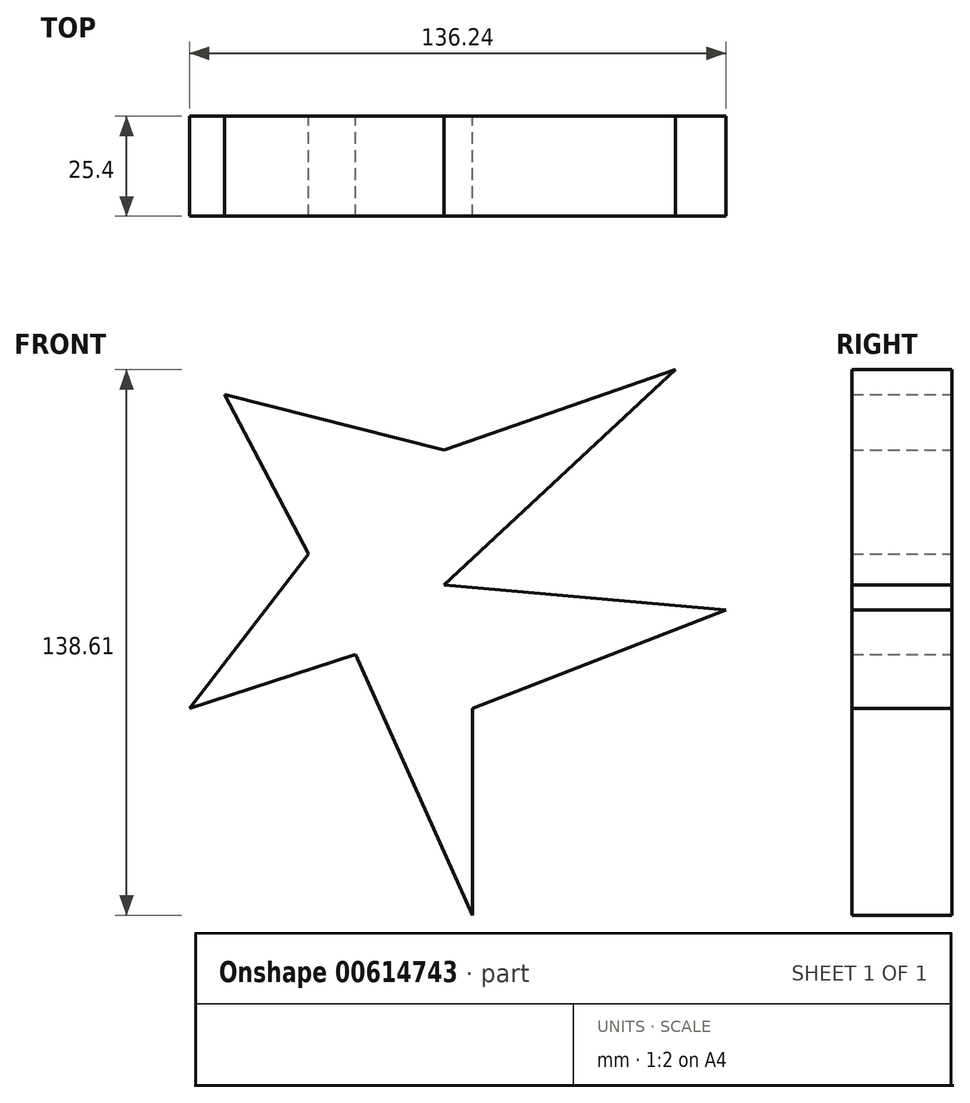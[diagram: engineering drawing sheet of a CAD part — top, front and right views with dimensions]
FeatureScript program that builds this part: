
annotation { "Feature Type Name" : "Feature", "Feature Type Description" : "" }
export const myFeature = defineFeature(function(context is Context, id is Id, definition is map)
    precondition{}
    {
        {
            var Q0;
            Q0=qCreatedBy(makeId("Front.planeOp"),FACE);
            var sketch = newSketch(context, id + "F0", { "sketchPlane" : qUnion([Q0])});
            skLineSegment(sketch, "E0", {"start": v(0, 0) * mm, "end": v(58.9, 54.64) * mm});
            skLineSegment(sketch, "E1", {"start": v(58.9, 54.64) * mm, "end": v(0, 34.3) * mm});
            skLineSegment(sketch, "E2", {"start": v(0, 34.3) * mm, "end": v(-57.95, 48.96) * mm});
            skLineSegment(sketch, "E3", {"start": v(-55.71, 48.4) * mm, "end": v(-34.3, 7.8) * mm});
            skLineSegment(sketch, "E4", {"start": v(-34.3, 7.8) * mm, "end": v(-64.57, -31.46) * mm});
            skLineSegment(sketch, "E5", {"start": v(-64.57, -31.46) * mm, "end": v(-22.47, -17.74) * mm});
            skLineSegment(sketch, "E6", {"start": v(-22.47, -17.74) * mm, "end": v(7.33, -83.97) * mm});
            skLineSegment(sketch, "E7", {"start": v(7.33, -83.97) * mm, "end": v(7.33, -31.46) * mm});
            skLineSegment(sketch, "E8", {"start": v(7.33, -31.46) * mm, "end": v(71.67, -6.39) * mm});
            skLineSegment(sketch, "E9", {"start": v(0, 0) * mm, "end": v(71.67, -6.39) * mm});
            skSolve(sketch);
        }
        {
            var Q0;
            Q0=makeQuery(id+"F0.imprint","IMPRINT",FACE,{"disambiguationData":[TD([[makeQuery(id+"F0.imprint","IMPRINT",EDGE,{"derivedFrom":sQuery(id+"F0.wireOp",EDGE,"E0")}),1.0]])]});
            extrude(context, id + "F1", {"entities" : qUnion([Q0]), "depth" : 25.4 * mm, "offsetDistance" : 25.4 * mm});
        }
    });
